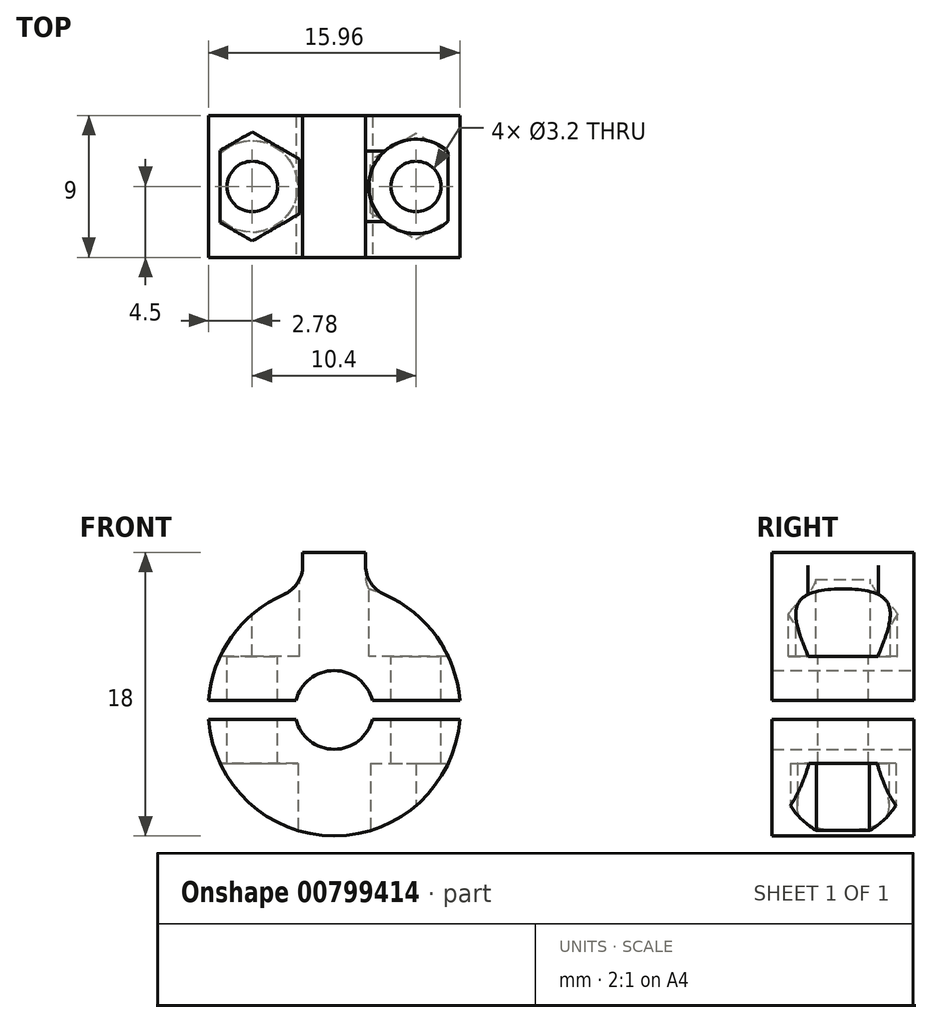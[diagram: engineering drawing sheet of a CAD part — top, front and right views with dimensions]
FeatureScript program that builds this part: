
annotation { "Feature Type Name" : "Feature", "Feature Type Description" : "" }
export const myFeature = defineFeature(function(context is Context, id is Id, definition is map)
    precondition{}
    {
        {
            var Q0;
            Q0=qCreatedBy(makeId("Front.planeOp"),FACE);
            var sketch = newSketch(context, id + "F0", { "sketchPlane" : qUnion([Q0])});
            skCircle(sketch, "E0", {"center": v(0, 0) * mm, "radius": 8 * mm});
            skCircle(sketch, "E1", {"center": v(0, 0) * mm, "radius": 2.5 * mm});
            skSolve(sketch);
        }
        {
            var Q0;
            Q0=makeQuery(id+"F0.imprint","IMPRINT",FACE,{"disambiguationData":[TD([[makeQuery(id+"F0.imprint","IMPRINT",EDGE,{"derivedFrom":sQuery(id+"F0.wireOp",EDGE,"E0")}),1.0]])]});
            extrude(context, id + "F1", {"entities" : qUnion([Q0]), "endBound" : BoundingType.SYMMETRIC, "depth" : 9 * mm, "offsetDistance" : 25 * mm});
        }
        {
            var Q0;
            Q0=qCreatedBy(makeId("Top.planeOp"),FACE);
            cPlane(context, id + "F2", {"entities" : qUnion([Q0]), "cplaneType" : CPlaneType.OFFSET, "offset" : 8 * mm, "width" : 150 * mm, "height" : 150 * mm});
        }
        {
            var Q0;
            Q0=makeQuery(id+"F1.opExtrude","CAP_FACE",FACE,{"disambiguationData":[OSD([sQuery(id+"F0.wireOp",EDGE,"E0"),sQuery(id+"F0.wireOp",EDGE,"E1")])],"isStart":false});
            var sketch = newSketch(context, id + "F3", { "sketchPlane" : qUnion([Q0])});
            skLineSegment(sketch, "E2.bottom", {"start": v(-8, -0.6) * mm, "end": v(8, -0.6) * mm});
            skLineSegment(sketch, "E2.top", {"start": v(-8, 0.6) * mm, "end": v(8, 0.6) * mm});
            skLineSegment(sketch, "E2.left", {"start": v(-8, -0.6) * mm, "end": v(-8, 0.6) * mm});
            skLineSegment(sketch, "E2.right", {"start": v(8, -0.6) * mm, "end": v(8, 0.6) * mm});
            skPoint(sketch, "E2.middle", {"position": v(0, 0) * mm});
            skSolve(sketch);
        }
        {
            var Q0;
            {var subQ1=makeQuery(id+"F1.opExtrude","CAP_EDGE",EDGE,{"disambiguationData":[OSD([sQuery(id+"F0.wireOp",EDGE,"E0")])],"isStart":false});var subQ4=sQuery(id+"F3.wireOp",EDGE,"E2.bottom");var subQ5=makeQuery(id+"F3.imprint","INTERSECT",VERTEX,{"disambiguationData":[OD(0.0)],"derivedFrom":[subQ1,subQ4]});Q0=makeQuery(id+"F3.imprint","IMPRINT",FACE,{"disambiguationData":[TD([[makeQuery(id+"F3.imprint","IMPRINT",EDGE,{"disambiguationData":[TD([[subQ5,-1.0]])],"derivedFrom":subQ4}),1.0]])]});}
            var Q1;
            {var subQ1=makeQuery(id+"F1.opExtrude","CAP_EDGE",EDGE,{"disambiguationData":[OSD([sQuery(id+"F0.wireOp",EDGE,"E0")])],"isStart":false});var subQ6=sQuery(id+"F3.wireOp",EDGE,"E2.bottom");var subQ7=makeQuery(id+"F3.imprint","INTERSECT",VERTEX,{"disambiguationData":[OD(1.0)],"derivedFrom":[subQ1,subQ6]});Q1=makeQuery(id+"F3.imprint","IMPRINT",FACE,{"disambiguationData":[TD([[makeQuery(id+"F3.imprint","IMPRINT",EDGE,{"disambiguationData":[TD([[subQ7,1.0]])],"derivedFrom":subQ6}),1.0]])]});}
            var Q2;
            Q2=makeQuery(id+"F1.opExtrude","CAP_FACE",FACE,{"disambiguationData":[OSD([sQuery(id+"F0.wireOp",EDGE,"E0"),sQuery(id+"F0.wireOp",EDGE,"E1")])],"isStart":true});
            extrude(context, id + "F4", {"entities" : qUnion([Q0, Q1]), "operationType" : NewBodyOperationType.REMOVE, "endBound" : BoundingType.UP_TO_SURFACE, "oppositeDirection" : true, "depth" : 25 * mm, "endBoundEntityFace" : qUnion([Q2]), "offsetDistance" : 25 * mm});
        }
        {
            var Q0;
            Q0=qCreatedBy(id+"F2.planeOp",FACE);
            var sketch = newSketch(context, id + "F5", { "sketchPlane" : qUnion([Q0])});
            skCircle(sketch, "E3", {"center": v(5.2, 0) * mm, "radius": 3 * mm});
            skCircle(sketch, "E4.cCircle", {"center": v(-5.2, 0) * mm, "radius": 3 * mm, "construction": true});
            skLineSegment(sketch, "E4.0", {"start": v(-8.2, -1.73) * mm, "end": v(-8.2, 1.73) * mm});
            skLineSegment(sketch, "E4.1", {"start": v(-8.2, 1.73) * mm, "end": v(-5.2, 3.46) * mm});
            skLineSegment(sketch, "E4.2", {"start": v(-5.2, 3.46) * mm, "end": v(-2.2, 1.73) * mm});
            skLineSegment(sketch, "E4.3", {"start": v(-2.2, 1.73) * mm, "end": v(-2.2, -1.73) * mm});
            skLineSegment(sketch, "E4.4", {"start": v(-2.2, -1.73) * mm, "end": v(-5.2, -3.46) * mm});
            skLineSegment(sketch, "E4.5", {"start": v(-5.2, -3.46) * mm, "end": v(-8.2, -1.73) * mm});
            skPoint(sketch, "E4.0.midPoint", {"position": v(-8.2, 0) * mm});
            skCircle(sketch, "E5", {"center": v(-5.2, 0) * mm, "radius": 1.6 * mm});
            skCircle(sketch, "E6", {"center": v(5.2, 0) * mm, "radius": 1.6 * mm});
            skSolve(sketch);
        }
        {
            var Q0;
            Q0=makeQuery(id+"F5.imprint","IMPRINT",FACE,{"disambiguationData":[TD([[makeQuery(id+"F5.imprint","IMPRINT",EDGE,{"derivedFrom":sQuery(id+"F5.wireOp",EDGE,"E4.0")}),-1.0]])]});
            var Q1;
            Q1=makeQuery(id+"F5.imprint","IMPRINT",FACE,{"disambiguationData":[TD([[makeQuery(id+"F5.imprint","IMPRINT",EDGE,{"derivedFrom":sQuery(id+"F5.wireOp",EDGE,"E3")}),1.0]])]});
            var Q2;
            {var subQ0=sQuery(id+"F3.wireOp",EDGE,"E2.top");Q2=makeQuery(id+"F4.boolean.opBoolean","COPY",FACE,{"derivedFrom":makeQuery(id+"F4.opExtrude","SWEPT_FACE",FACE,{"disambiguationData":[OSD([subQ0]),TDD([makeQuery(id+"F3.imprint","IMPRINT",EDGE,{"disambiguationData":[TD([[makeQuery(id+"F3.imprint","INTERSECT",VERTEX,{"disambiguationData":[OD(0.0)],"derivedFrom":[makeQuery(id+"F1.opExtrude","CAP_EDGE",EDGE,{"disambiguationData":[OSD([sQuery(id+"F0.wireOp",EDGE,"E0")])],"isStart":false}),subQ0]}),-1.0]])],"derivedFrom":subQ0})])]})});}
            extrude(context, id + "F6", {"entities" : qUnion([Q0, Q1]), "operationType" : NewBodyOperationType.REMOVE, "endBound" : BoundingType.UP_TO_SURFACE, "oppositeDirection" : true, "depth" : 25 * mm, "endBoundEntityFace" : qUnion([Q2]), "hasOffset" : true, "offsetDistance" : 2.8 * mm});
        }
        {
            var Q0;
            Q0=qCreatedBy(makeId("Top.planeOp"),FACE);
            cPlane(context, id + "F7", {"entities" : qUnion([Q0]), "cplaneType" : CPlaneType.OFFSET, "offset" : 8 * mm, "oppositeDirection" : true, "width" : 150 * mm, "height" : 150 * mm});
        }
        {
            var Q0;
            Q0=qCreatedBy(id+"F7.planeOp",FACE);
            var sketch = newSketch(context, id + "F8", { "sketchPlane" : qUnion([Q0])});
            skCircle(sketch, "E7", {"center": v(-5.2, 0) * mm, "radius": 2.9 * mm});
            skCircle(sketch, "E8.cCircle", {"center": v(5.2, 0) * mm, "radius": 2.9 * mm, "construction": true});
            skLineSegment(sketch, "E8.0", {"start": v(8.1, 1.67) * mm, "end": v(8.1, -1.67) * mm});
            skLineSegment(sketch, "E8.1", {"start": v(8.1, -1.67) * mm, "end": v(5.2, -3.35) * mm});
            skLineSegment(sketch, "E8.2", {"start": v(5.2, -3.35) * mm, "end": v(2.3, -1.67) * mm});
            skLineSegment(sketch, "E8.3", {"start": v(2.3, -1.67) * mm, "end": v(2.3, 1.67) * mm});
            skLineSegment(sketch, "E8.4", {"start": v(2.3, 1.67) * mm, "end": v(5.2, 3.35) * mm});
            skLineSegment(sketch, "E8.5", {"start": v(5.2, 3.35) * mm, "end": v(8.1, 1.67) * mm});
            skPoint(sketch, "E8.0.midPoint", {"position": v(8.1, 0) * mm});
            skCircle(sketch, "E9", {"center": v(5.2, 0) * mm, "radius": 1.6 * mm});
            skCircle(sketch, "E10", {"center": v(-5.2, 0) * mm, "radius": 1.6 * mm});
            skSolve(sketch);
        }
        {
            var Q0;
            Q0=makeQuery(id+"F8.imprint","IMPRINT",FACE,{"disambiguationData":[TD([[makeQuery(id+"F8.imprint","IMPRINT",EDGE,{"derivedFrom":sQuery(id+"F8.wireOp",EDGE,"E7")}),1.0]])]});
            var Q1;
            Q1=makeQuery(id+"F8.imprint","IMPRINT",FACE,{"disambiguationData":[TD([[makeQuery(id+"F8.imprint","IMPRINT",EDGE,{"derivedFrom":sQuery(id+"F8.wireOp",EDGE,"E8.0")}),-1.0]])]});
            var Q2;
            {var subQ0=sQuery(id+"F3.wireOp",EDGE,"E2.bottom");Q2=makeQuery(id+"F4.boolean.opBoolean","COPY",FACE,{"derivedFrom":makeQuery(id+"F4.opExtrude","SWEPT_FACE",FACE,{"disambiguationData":[OSD([subQ0]),TDD([makeQuery(id+"F3.imprint","IMPRINT",EDGE,{"disambiguationData":[TD([[makeQuery(id+"F3.imprint","INTERSECT",VERTEX,{"disambiguationData":[OD(1.0)],"derivedFrom":[makeQuery(id+"F1.opExtrude","CAP_EDGE",EDGE,{"disambiguationData":[OSD([sQuery(id+"F0.wireOp",EDGE,"E0")])],"isStart":false}),subQ0]}),1.0]])],"derivedFrom":subQ0})])]})});}
            extrude(context, id + "F9", {"entities" : qUnion([Q0, Q1]), "operationType" : NewBodyOperationType.REMOVE, "endBound" : BoundingType.UP_TO_SURFACE, "depth" : 25 * mm, "endBoundEntityFace" : qUnion([Q2]), "hasOffset" : true, "offsetDistance" : 2.8 * mm});
        }
        {
            var Q0;
            Q0=makeQuery(id+"F5.imprint","IMPRINT",FACE,{"disambiguationData":[TD([[makeQuery(id+"F5.imprint","IMPRINT",EDGE,{"derivedFrom":sQuery(id+"F5.wireOp",EDGE,"E5")}),1.0]])]});
            var Q1;
            Q1=makeQuery(id+"F5.imprint","IMPRINT",FACE,{"disambiguationData":[TD([[makeQuery(id+"F5.imprint","IMPRINT",EDGE,{"derivedFrom":sQuery(id+"F5.wireOp",EDGE,"E6")}),1.0]])]});
            extrude(context, id + "F10", {"entities" : qUnion([Q0, Q1]), "operationType" : NewBodyOperationType.REMOVE, "oppositeDirection" : true, "depth" : 25 * mm, "offsetDistance" : 25 * mm});
        }
        {
            var Q0;
            Q0=qCreatedBy(makeId("Top.planeOp"),FACE);
            cPlane(context, id + "F11", {"entities" : qUnion([Q0]), "cplaneType" : CPlaneType.OFFSET, "offset" : 5 * mm, "width" : 150 * mm, "height" : 150 * mm});
        }
        {
            var Q0;
            Q0=qCreatedBy(id+"F11.planeOp",FACE);
            var sketch = newSketch(context, id + "F12", { "sketchPlane" : qUnion([Q0])});
            skLineSegment(sketch, "E11.0", {"start": v(7.98, -4.5) * mm, "end": v(-7.98, -4.5) * mm, "construction": true});
            skLineSegment(sketch, "E12.bottom", {"start": v(-2, -4.5) * mm, "end": v(2, -4.5) * mm});
            skLineSegment(sketch, "E12.top", {"start": v(-2, 4.5) * mm, "end": v(2, 4.5) * mm});
            skLineSegment(sketch, "E12.left", {"start": v(-2, -4.5) * mm, "end": v(-2, 4.5) * mm});
            skLineSegment(sketch, "E12.right", {"start": v(2, -4.5) * mm, "end": v(2, 4.5) * mm});
            skPoint(sketch, "E12.middle", {"position": v(0, 0) * mm});
            skSolve(sketch);
        }
        {
            var Q0;
            Q0 = qSketchRegion(id + "F12", true);
            extrude(context, id + "F13", {"entities" : qUnion([Q0]), "operationType" : NewBodyOperationType.ADD, "depth" : 5 * mm, "offsetDistance" : 25 * mm});
        }
        {
            var Q0;
            {var subQ1=sQuery(id+"F0.wireOp",EDGE,"E0");var subQ3=sQuery(id+"F3.wireOp",EDGE,"E2.top");var subQ4=makeQuery(id+"F1.opExtrude","CAP_EDGE",EDGE,{"disambiguationData":[OSD([subQ1])],"isStart":false});var subQ7=makeQuery(id+"F4.opExtrude","SWEPT_FACE",FACE,{"disambiguationData":[OSD([subQ3]),TDD([makeQuery(id+"F3.imprint","IMPRINT",EDGE,{"disambiguationData":[TD([[makeQuery(id+"F3.imprint","INTERSECT",VERTEX,{"disambiguationData":[OD(0.0)],"derivedFrom":[subQ4,subQ3]}),-1.0]])],"derivedFrom":subQ3})])]});Q0=makeQuery(id+"F13.boolean.opBoolean","INTERSECT",EDGE,{"derivedFrom":[makeQuery(id+"F6.boolean.opBoolean","SPLIT",FACE,{"disambiguationData":[TD([makeQuery(id+"F6.opExtrude","SWEPT_FACE",FACE,{"disambiguationData":[OSD([sQuery(id+"F5.wireOp",EDGE,"E3")])]})])],"derivedFrom":makeQuery(id+"F4.boolean.opBoolean","SPLIT",FACE,{"disambiguationData":[TD([subQ7])],"derivedFrom":makeQuery(id+"F1.opExtrude","SWEPT_FACE",FACE,{"disambiguationData":[OSD([subQ1])]})})}),makeQuery(id+"F13.opExtrude","SWEPT_FACE",FACE,{"disambiguationData":[OSD([sQuery(id+"F12.wireOp",EDGE,"E12.left")])]})]});}
            var Q1;
            {var subQ1=sQuery(id+"F0.wireOp",EDGE,"E0");var subQ3=sQuery(id+"F3.wireOp",EDGE,"E2.top");var subQ4=makeQuery(id+"F1.opExtrude","CAP_EDGE",EDGE,{"disambiguationData":[OSD([subQ1])],"isStart":false});var subQ7=makeQuery(id+"F4.opExtrude","SWEPT_FACE",FACE,{"disambiguationData":[OSD([subQ3]),TDD([makeQuery(id+"F3.imprint","IMPRINT",EDGE,{"disambiguationData":[TD([[makeQuery(id+"F3.imprint","INTERSECT",VERTEX,{"disambiguationData":[OD(0.0)],"derivedFrom":[subQ4,subQ3]}),-1.0]])],"derivedFrom":subQ3})])]});Q1=makeQuery(id+"F13.boolean.opBoolean","INTERSECT",EDGE,{"derivedFrom":[makeQuery(id+"F6.boolean.opBoolean","SPLIT",FACE,{"disambiguationData":[TD([makeQuery(id+"F6.opExtrude","SWEPT_FACE",FACE,{"disambiguationData":[OSD([sQuery(id+"F5.wireOp",EDGE,"E3")])]})])],"derivedFrom":makeQuery(id+"F4.boolean.opBoolean","SPLIT",FACE,{"disambiguationData":[TD([subQ7])],"derivedFrom":makeQuery(id+"F1.opExtrude","SWEPT_FACE",FACE,{"disambiguationData":[OSD([subQ1])]})})}),makeQuery(id+"F13.opExtrude","SWEPT_FACE",FACE,{"disambiguationData":[OSD([sQuery(id+"F12.wireOp",EDGE,"E12.right")])]})]});}
            fillet(context, id + "F14", {"entities" : qUnion([Q0, Q1]), "radius" : 2 * mm, "tangentPropagation" : true, "allowEdgeOverflow" : false});
        }
    });
